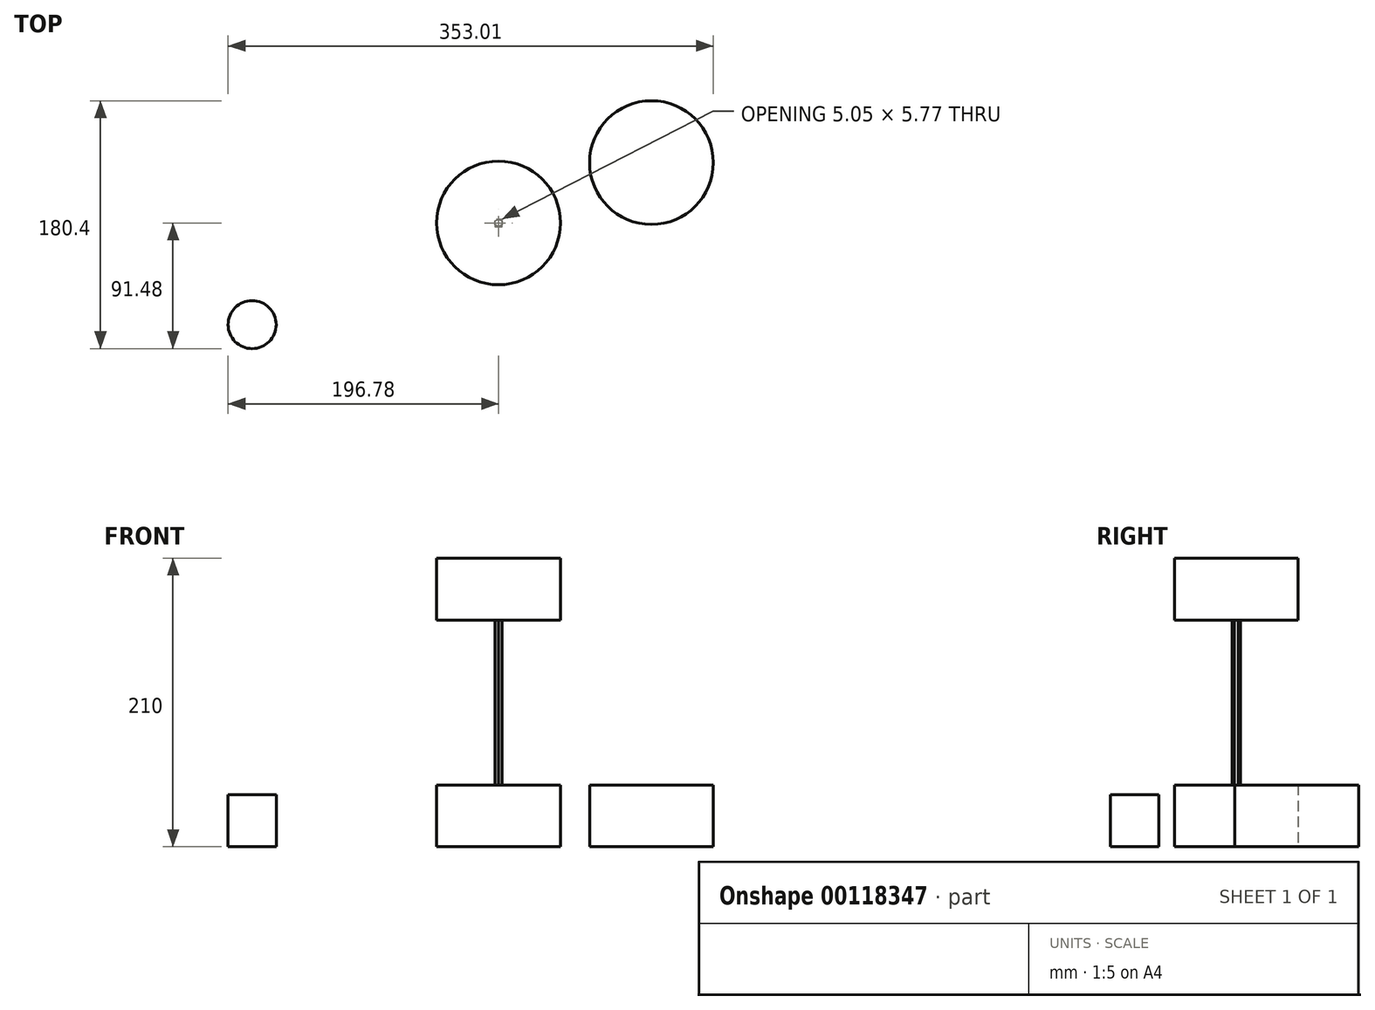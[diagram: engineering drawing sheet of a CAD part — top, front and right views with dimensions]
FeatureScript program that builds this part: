
annotation { "Feature Type Name" : "Feature", "Feature Type Description" : "" }
export const myFeature = defineFeature(function(context is Context, id is Id, definition is map)
    precondition{}
    {
        {
            var Q0;
            Q0=qCreatedBy(makeId("Top.planeOp"),FACE);
            var sketch = newSketch(context, id + "F0", { "sketchPlane" : qUnion([Q0])});
            skCircle(sketch, "E0", {"center": v(0, 0) * mm, "radius": 45 * mm});
            skSolve(sketch);
        }
        {
            var Q0;
            Q0 = qSketchRegion(id + "F0", true);
            extrude(context, id + "F1", {"entities" : qUnion([Q0]), "depth" : 45 * mm});
        }
        {
            var Q0;
            Q0=makeQuery(id+"F1.opExtrude","CAP_FACE",FACE,{"disambiguationData":[OSD([sQuery(id+"F0.wireOp",EDGE,"E0")])],"isStart":false});
            var sketch = newSketch(context, id + "F2", { "sketchPlane" : qUnion([Q0])});
            skCircle(sketch, "E1.cCircle", {"center": v(0, 0) * mm, "radius": 2.5 * mm, "construction": true});
            skLineSegment(sketch, "E1.0", {"start": v(-0.05, 2.89) * mm, "end": v(2.48, 1.48) * mm});
            skLineSegment(sketch, "E1.1", {"start": v(2.48, 1.48) * mm, "end": v(2.52, -1.4) * mm});
            skLineSegment(sketch, "E1.2", {"start": v(2.52, -1.4) * mm, "end": v(0.05, -2.89) * mm});
            skLineSegment(sketch, "E1.3", {"start": v(0.05, -2.89) * mm, "end": v(-2.48, -1.48) * mm});
            skLineSegment(sketch, "E1.4", {"start": v(-2.48, -1.48) * mm, "end": v(-2.52, 1.4) * mm});
            skLineSegment(sketch, "E1.5", {"start": v(-2.52, 1.4) * mm, "end": v(-0.05, 2.89) * mm});
            skPoint(sketch, "E1.0.midPoint", {"position": v(1.22, 2.18) * mm});
            skSolve(sketch);
        }
        {
            var Q0;
            Q0 = qSketchRegion(id + "F2", true);
            extrude(context, id + "F3", {"entities" : qUnion([Q0]), "operationType" : NewBodyOperationType.ADD, "depth" : 120 * mm});
        }
        {
            var Q0;
            Q0=makeQuery(id+"F3.opExtrude","CAP_FACE",FACE,{"disambiguationData":[OSD([sQuery(id+"F2.wireOp",EDGE,"E1.0"),sQuery(id+"F2.wireOp",EDGE,"E1.1"),sQuery(id+"F2.wireOp",EDGE,"E1.2"),sQuery(id+"F2.wireOp",EDGE,"E1.3"),sQuery(id+"F2.wireOp",EDGE,"E1.4"),sQuery(id+"F2.wireOp",EDGE,"E1.5")])],"isStart":false});
            var sketch = newSketch(context, id + "F4", { "sketchPlane" : qUnion([Q0])});
            skCircle(sketch, "E2", {"center": v(0, 0) * mm, "radius": 45 * mm});
            skSolve(sketch);
        }
        {
            var Q0;
            Q0 = qSketchRegion(id + "F4", true);
            extrude(context, id + "F5", {"entities" : qUnion([Q0]), "operationType" : NewBodyOperationType.ADD, "depth" : 45 * mm});
        }
        {
            var Q0;
            Q0=qCreatedBy(makeId("Top.planeOp"),FACE);
            var sketch = newSketch(context, id + "F6", { "sketchPlane" : qUnion([Q0])});
            skCircle(sketch, "E3", {"center": v(111.23, 43.92) * mm, "radius": 45 * mm});
            skSolve(sketch);
        }
        {
            var Q0;
            Q0 = qSketchRegion(id + "F6", true);
            extrude(context, id + "F7", {"entities" : qUnion([Q0]), "depth" : 45 * mm});
        }
        {
            var Q0;
            Q0=qCreatedBy(makeId("Top.planeOp"),FACE);
            var sketch = newSketch(context, id + "F8", { "sketchPlane" : qUnion([Q0])});
            skCircle(sketch, "E4", {"center": v(-179.28, -73.98) * mm, "radius": 17.5 * mm});
            skSolve(sketch);
        }
        {
            var Q0;
            Q0 = qSketchRegion(id + "F8", true);
            extrude(context, id + "F9", {"entities" : qUnion([Q0]), "depth" : 38 * mm});
        }
    });
